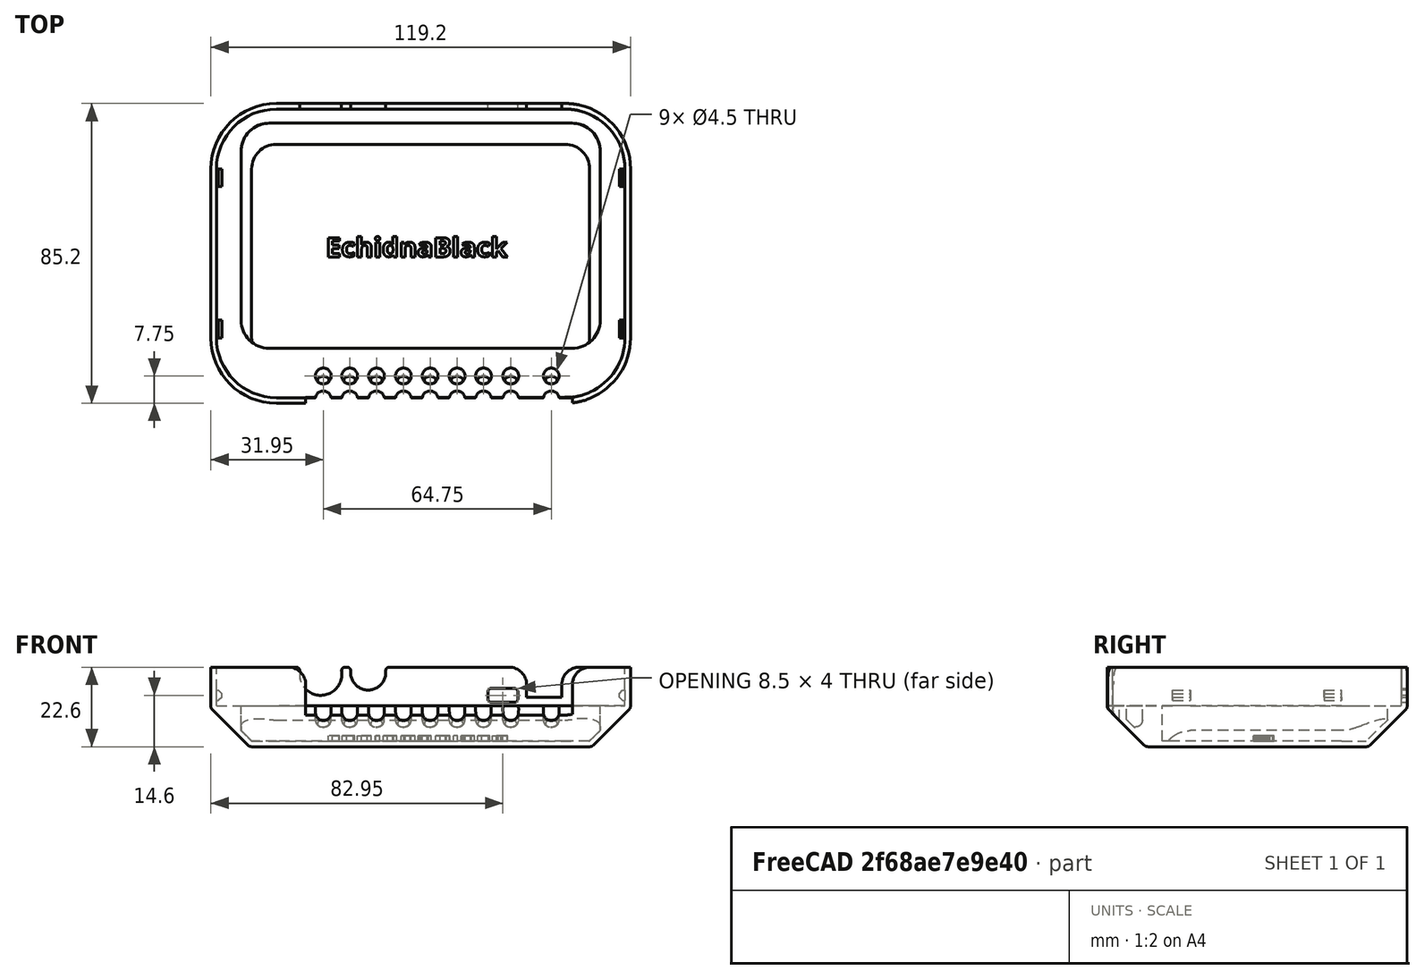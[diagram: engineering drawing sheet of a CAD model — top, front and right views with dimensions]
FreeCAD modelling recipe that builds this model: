
FCSTD DOCUMENT  (FreeCAD 0.18R4 (GitTag))
Label: Caixa_EchidaBlack
License: All rights reserved
LicenseURL: http://en.wikipedia.org/wiki/All_rights_reserved
objects: Part::Cylinder×23, Part::Fillet×16, Part::Box×13, Part::Cut×12, Part::Chamfer×6, Part::MultiFuse×5, Part::Thickness×3, Part::Part2DObjectPython×1, Part::Extrusion×1
note: 80 computed .brp shape members not serialized (recipe doc carries the construction recipe); baked Part::Feature solids carry a one-line shape summary decoded from their .brp

FEATURE [Part::Box] Box002  label="Cubo002"
  AttacherType = Attacher::AttachEngine3D
  Height = 21
  Length = 116
  Placement = pos=(-5.1,-1,-12) rot=(0,0,1;0rad)
  Width = 82
FEATURE [Part::Fillet] Fillet
  Base = -> Box002
  Edges = 1 edges r=17: [Edge3]
FEATURE [Part::Fillet] Fillet001
  Base = -> Fillet
  Edges = 1 edges r=17: [Edge15]
FEATURE [Part::Fillet] Fillet002
  Base = -> Fillet001
  Edges = 1 edges r=17: [Edge16]
FEATURE [Part::Fillet] Fillet003
  Base = -> Fillet002
  Edges = 1 edges r=17: [Edge16]
FEATURE [Part::Box] Box006  label="Cubo006"
  AttacherType = Attacher::AttachEngine3D
  Height = 9
  Length = 10
  Placement = pos=(83,76,0.5) rot=(0,0,1;0rad)
  Width = 8
FEATURE [Part::Box] Box013  label="Cubo013"
  AttacherType = Attacher::AttachEngine3D
  Height = 12
  Length = 75.75
  Placement = pos=(20.25,-4,-2) rot=(0,0,1;0rad)
  Width = 10
FEATURE [Part::Cylinder] Cylinder005  label="Cilindro005"
  Angle = 360
  AttacherType = Attacher::AttachEngine3D
  Height = 12
  Placement = pos=(32.75,5.15,-9) rot=(0,0,1;0rad)
  Radius = 2.25
FEATURE [Part::Cylinder] Cylinder006  label="Cilindro006"
  Angle = 360
  AttacherType = Attacher::AttachEngine3D
  Height = 12
  Placement = pos=(25.25,5.15,-9) rot=(0,0,1;0rad)
  Radius = 2.25
FEATURE [Part::Cylinder] Cylinder007  label="Cilindro007"
  Angle = 360
  AttacherType = Attacher::AttachEngine3D
  Height = 12
  Placement = pos=(40.35,5.15,-9) rot=(0,0,1;0rad)
  Radius = 2.25
FEATURE [Part::Cylinder] Cylinder008  label="Cilindro008"
  Angle = 360
  AttacherType = Attacher::AttachEngine3D
  Height = 12
  Placement = pos=(48,5.15,-9) rot=(0,0,1;0rad)
  Radius = 2.25
FEATURE [Part::Cylinder] Cylinder009  label="Cilindro009"
  Angle = 360
  AttacherType = Attacher::AttachEngine3D
  Height = 12
  Placement = pos=(55.6,5.15,-9) rot=(0,0,1;0rad)
  Radius = 2.25
FEATURE [Part::Cylinder] Cylinder010  label="Cilindro010"
  Angle = 360
  AttacherType = Attacher::AttachEngine3D
  Height = 12
  Placement = pos=(63.25,5.15,-9) rot=(0,0,1;0rad)
  Radius = 2.25
FEATURE [Part::Cylinder] Cylinder011  label="Cilindro011"
  Angle = 360
  AttacherType = Attacher::AttachEngine3D
  Height = 12
  Placement = pos=(70.75,5.15,-9) rot=(0,0,1;0rad)
  Radius = 2.25
FEATURE [Part::Cylinder] Cylinder012  label="Cilindro012"
  Angle = 360
  AttacherType = Attacher::AttachEngine3D
  Height = 12
  Placement = pos=(70.75,5.15,-9) rot=(0,0,1;0rad)
  Radius = 2.25
FEATURE [Part::Cylinder] Cylinder013  label="Cilindro013"
  Angle = 360
  AttacherType = Attacher::AttachEngine3D
  Height = 12
  Placement = pos=(78.5,5.15,-9) rot=(0,0,1;0rad)
  Radius = 2.25
FEATURE [Part::Cylinder] Cylinder014  label="Cilindro014"
  Angle = 360
  AttacherType = Attacher::AttachEngine3D
  Height = 12
  Placement = pos=(90,5.15,-9) rot=(0,0,1;0rad)
  Radius = 2.25
FEATURE [Part::MultiFuse] Fusion  label="FusionCilindros"
  Shapes = -> [Cylinder005,Cylinder006,Cylinder009,Cylinder013,Cylinder011,Cylinder012,Cylinder007,Cylinder008,Cylinder010,Cylinder014]
FEATURE [Part::Part2DObjectPython] ShapeString  # Draft 2D object (typed FeaturePython)
  FontFile = <path>
  MapMode = 5
  Placement = pos=(26,39,-11) rot=(0,0,1;0rad)
  Size = 7
  String = EchidnaBlack
  Tracking = 0
FEATURE [Part::Box] Box014  label="Cubo014"
  AttacherType = Attacher::AttachEngine3D
  Height = 10
  Length = 116
  Placement = pos=(-5.1,-1,-17) rot=(0,0,1;0rad)
  Width = 82
FEATURE [Part::Fillet] Fillet022
  Base = -> Box014
  Edges = 1 edges r=17: [Edge7]
FEATURE [Part::Fillet] Fillet023
  Base = -> Fillet022
  Edges = 3 edges r=17: [Edge3,Edge12,Edge15]
  Placement = pos=(0,0,11) rot=(0,0,1;0rad)
FEATURE [Part::Box] Box015  label="Cubo015"
  AttacherType = Attacher::AttachEngine3D
  Height = 10
  Length = 102
  Placement = pos=(1.9,13,-12) rot=(0,0,1;0rad)
  Width = 64
FEATURE [Part::Fillet] Fillet024
  Base = -> Box015
  Edges = 4 edges r=8: [Edge1,Edge3,Edge5,Edge7]
  Placement = pos=(0,0,6) rot=(0,0,1;0rad)
FEATURE [Part::Box] Box016  label="Cubo016"
  AttacherType = Attacher::AttachEngine3D
  Height = 4
  Length = 8.5
  Placement = pos=(72,75,-1) rot=(0,0,1;0rad)
  Width = 8
FEATURE [Part::Cylinder] Cylinder  label="Cilindro"
  Angle = 360
  AttacherType = Attacher::AttachEngine3D
  Height = 10
  Placement = pos=(38,88,7.5) rot=(1,0,0;1.5708rad)
  Radius = 5
FEATURE [Part::Cylinder] Cylinder025  label="Cilindro025"
  Angle = 360
  AttacherType = Attacher::AttachEngine3D
  Height = 10
  Placement = pos=(24.5,88,7) rot=(1,0,0;1.5708rad)
  Radius = 6
FEATURE [Part::Box] Box  label="Cubo"
  AttacherType = Attacher::AttachEngine3D
  Height = 3
  Length = 2
  Placement = pos=(-5.25,27,-2) rot=(0,0,1;0rad)
  Width = 5
FEATURE [Part::Box] Box017  label="Cubo017"
  AttacherType = Attacher::AttachEngine3D
  Height = 3
  Length = 2
  Placement = pos=(109,27,-2) rot=(0,0,1;0rad)
  Width = 5
FEATURE [Part::Chamfer] Chamfer001
  Base = -> Box017
  Edges = 2 edges r=1: [Edge2,Edge4]
  Placement = pos=(0.3,-11,1.5) rot=(0,0,1;0rad)
FEATURE [Part::Box] Box018  label="Cubo018"
  AttacherType = Attacher::AttachEngine3D
  Height = 3
  Length = 2
  Placement = pos=(-5.25,27,-2) rot=(0,0,1;0rad)
  Width = 5
FEATURE [Part::Chamfer] Chamfer002
  Base = -> Box018
  Edges = 2 edges r=1: [Edge6,Edge8]
  Placement = pos=(-0.3,32,1.5) rot=(0,0,1;0rad)
FEATURE [Part::Box] Box019  label="Cubo019"
  AttacherType = Attacher::AttachEngine3D
  Height = 3
  Length = 2
  Placement = pos=(109,27,-2) rot=(0,0,1;0rad)
  Width = 5
FEATURE [Part::Chamfer] Chamfer003
  Base = -> Box019
  Edges = 2 edges r=1: [Edge2,Edge4]
  Placement = pos=(0.3,32,1.5) rot=(0,0,1;0rad)
FEATURE [Part::Fillet] Fillet028
  Base = -> Box016
  Edges = 4 edges r=1: [Edge2,Edge4,Edge6,Edge8]
  Placement = pos=(0,1,0) rot=(0,0,1;0rad)
FEATURE [Part::Cut] Cut
  Base = -> Fillet023
  Placement = pos=(0,0,-6) rot=(0,0,1;0rad)
  Tool = -> Fillet024
FEATURE [Part::Cylinder] Cylinder036  label="Cilindro036"
  Angle = 360
  AttacherType = Attacher::AttachEngine3D
  Height = 12
  Placement = pos=(70.75,5.15,-9) rot=(0,0,1;0rad)
  Radius = 2.25
FEATURE [Part::Cylinder] Cylinder037  label="Cilindro037"
  Angle = 360
  AttacherType = Attacher::AttachEngine3D
  Height = 12
  Placement = pos=(70.75,5.15,-9) rot=(0,0,1;0rad)
  Radius = 2.25
FEATURE [Part::Cylinder] Cylinder038  label="Cilindro038"
  Angle = 360
  AttacherType = Attacher::AttachEngine3D
  Height = 12
  Placement = pos=(78.5,5.15,-9) rot=(0,0,1;0rad)
  Radius = 2.25
FEATURE [Part::Cylinder] Cylinder039  label="Cilindro039"
  Angle = 360
  AttacherType = Attacher::AttachEngine3D
  Height = 12
  Placement = pos=(90,5.15,-9) rot=(0,0,1;0rad)
  Radius = 2.25
FEATURE [Part::Cylinder] Cylinder040  label="Cilindro040"
  Angle = 360
  AttacherType = Attacher::AttachEngine3D
  Height = 12
  Placement = pos=(32.75,5.15,-9) rot=(0,0,1;0rad)
  Radius = 2.25
FEATURE [Part::Cylinder] Cylinder041  label="Cilindro041"
  Angle = 360
  AttacherType = Attacher::AttachEngine3D
  Height = 12
  Placement = pos=(25.25,5.15,-9) rot=(0,0,1;0rad)
  Radius = 2.25
FEATURE [Part::Cylinder] Cylinder042  label="Cilindro042"
  Angle = 360
  AttacherType = Attacher::AttachEngine3D
  Height = 12
  Placement = pos=(40.35,5.15,-9) rot=(0,0,1;0rad)
  Radius = 2.25
FEATURE [Part::Cylinder] Cylinder043  label="Cilindro043"
  Angle = 360
  AttacherType = Attacher::AttachEngine3D
  Height = 12
  Placement = pos=(48,5.15,-9) rot=(0,0,1;0rad)
  Radius = 2.25
FEATURE [Part::Cylinder] Cylinder044  label="Cilindro044"
  Angle = 360
  AttacherType = Attacher::AttachEngine3D
  Height = 12
  Placement = pos=(55.6,5.15,-9) rot=(0,0,1;0rad)
  Radius = 2.25
FEATURE [Part::Cylinder] Cylinder045  label="Cilindro045"
  Angle = 360
  AttacherType = Attacher::AttachEngine3D
  Height = 12
  Placement = pos=(63.25,5.15,-9) rot=(0,0,1;0rad)
  Radius = 2.25
FEATURE [Part::MultiFuse] Fusion003  label="FusionCilindros002"
  Placement = pos=(0,-6.5,1) rot=(0,0,1;0rad)
  Shapes = -> [Cylinder040,Cylinder041,Cylinder044,Cylinder038,Cylinder036,Cylinder037,Cylinder042,Cylinder043,Cylinder045,Cylinder039]
FEATURE [Part::Chamfer] Chamfer004
  Base = -> Fillet003
  Edges = 8 edges r=10: [Edge9,Edge12,Edge14,Edge17,Edge19,Edge20,Edge22,Edge24]
FEATURE [Part::Thickness] Thickness
  Faces = -> Chamfer004 [Face4]
  Intersection = false
  Join = 0
  Mode = 0
  SelfIntersection = false
  Value = 1.6
FEATURE [Part::Box] Box020  label="Cubo020"
  AttacherType = Attacher::AttachEngine3D
  Height = 21
  Length = 116
  Placement = pos=(-5.1,-1,-12) rot=(0,0,1;0rad)
  Width = 82
FEATURE [Part::Fillet] Fillet030
  Base = -> Box020
  Edges = 1 edges r=17: [Edge3]
FEATURE [Part::Fillet] Fillet029
  Base = -> Fillet030
  Edges = 1 edges r=17: [Edge15]
FEATURE [Part::Fillet] Fillet031
  Base = -> Fillet029
  Edges = 1 edges r=17: [Edge16]
FEATURE [Part::Fillet] Fillet032
  Base = -> Fillet031
  Edges = 1 edges r=17: [Edge16]
FEATURE [Part::Chamfer] Chamfer005
  Base = -> Fillet032
  Edges = 8 edges r=10: [Edge9,Edge12,Edge14,Edge17,Edge19,Edge20,Edge22,Edge24]
FEATURE [Part::Thickness] Thickness001
  Faces = -> Chamfer005 [Face4]
  Intersection = false
  Join = 0
  Mode = 0
  SelfIntersection = false
  Value = 10
FEATURE [Part::Cut] Cut010  label="SoportePCB"
  Base = -> Cut
  Tool = -> Thickness001
FEATURE [Part::Fillet] Fillet033  label="Cilindros 1"
  Base = -> Fusion
  Edges = 9 edges r=2: [Edge2,Edge6,Edge9,Edge12,Edge15,Edge18,Edge21,Edge24,Edge27]
  Placement = pos=(0,0,1) rot=(0,0,1;0rad)
FEATURE [Part::Cylinder] Cylinder046  label="Cilindro046"
  Angle = 120
  AttacherType = Attacher::AttachEngine3D
  Height = 76
  Placement = pos=(20,-2,-2) rot=(0,1,0;1.5708rad)
  Radius = 4
FEATURE [Part::Thickness] Thickness002
  Faces = -> Cylinder046 [Face4,Face5]
  Intersection = false
  Join = 0
  Mode = 0
  Placement = pos=(0,0,6) rot=(0,0,1;3.14159rad)
  SelfIntersection = false
  Value = 2
FEATURE [Part::Box] Box021  label="Cubo021"
  AttacherType = Attacher::AttachEngine3D
  Height = 25
  Length = 5
  Placement = pos=(-20.255,-11,-9) rot=(0,0,1;0rad)
  Width = 17
FEATURE [Part::Box] Box022  label="Cubo022"
  AttacherType = Attacher::AttachEngine3D
  Height = 25
  Length = 5
  Placement = pos=(-101,-11,-9) rot=(0,0,1;0rad)
  Width = 17
FEATURE [Part::Cut] Cut013
  Base = -> Thickness002
  Tool = -> Box021
FEATURE [Part::Cut] Cut014  label="Cilindro_chaflan"
  Base = -> Cut013
  Placement = pos=(0,1,1) rot=(0,1,0;3.14159rad)
  Tool = -> Box022
FEATURE [Part::Chamfer] Chamfer
  Base = -> Box
  Edges = 2 edges r=1: [Edge6,Edge8]
  Placement = pos=(-0.3,-11,1.5) rot=(0,0,1;0rad)
FEATURE [Part::Extrusion] Extrude  label="Texto"
  Base = -> ShapeString
  Dir = (0,0,1)
  DirMode = 2
  FaceMakerClass = Part::FaceMakerBullseye
  LengthFwd = 2
  LengthRev = 0
  Placement = pos=(0,0,-1.5) rot=(0,0,1;0rad)
  Solid = false
  Symmetric = false
FEATURE [Part::MultiFuse] Fusion006  label="aletas"
  Shapes = -> [Chamfer,Chamfer002,Chamfer001,Chamfer003]
FEATURE [Part::Cut] Cut015
  Base = -> Thickness
  Tool = -> Box013
FEATURE [Part::Cut] Cut016
  Base = -> Cut010
  Tool = -> Fillet033
FEATURE [Part::MultiFuse] Fusion007
  Shapes = -> [Cut015,Cut016]
FEATURE [Part::Cut] Cut017
  Base = -> Fusion007
  Tool = -> Fusion003
FEATURE [Part::Cut] Cut018
  Base = -> Cut017
  Tool = -> Cut014
FEATURE [Part::Cut] Cut019
  Base = -> Cut018
  Tool = -> Box006
FEATURE [Part::Cut] Cut020
  Base = -> Cut019
  Tool = -> Fillet028
FEATURE [Part::Cut] Cut021
  Base = -> Cut020
  Tool = -> Cylinder025
FEATURE [Part::Cut] Cut022
  Base = -> Cut021
  Tool = -> Cylinder
FEATURE [Part::Fillet] Fillet034
  Base = -> Cut022
  Edges = 2 edges r=5: [Edge2,Edge156]
FEATURE [Part::Fillet] Fillet035
  Base = -> Fillet034
  Edges = 2 edges r=5: [Edge255,Edge258]
FEATURE [Part::Fillet] Fillet036  label="Base"
  Base = -> Fillet035
  Edges = 4 edges r=1: [Edge91,Edge99,Edge102,Edge104]
FEATURE [Part::MultiFuse] Fusion008
  Shapes = -> [Fusion006,Fillet036,Extrude]
note: 1 file-system path scrubbed to <path> (originals preserved in the JSON sidecar)
